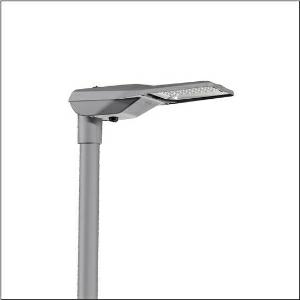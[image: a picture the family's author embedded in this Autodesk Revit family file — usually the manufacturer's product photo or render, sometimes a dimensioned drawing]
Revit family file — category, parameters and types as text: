
# Revit family: streetlight_sl_21_iq_mini___p0_5a_5xe2v31y08jb_f279
name_source: partatom
category: Lighting Fixtures
units: mm (PartAtom-declared; Revit-internal decimal feet)

## family parameters
Cut with Voids When Loaded = No
Host = Face
Light Source = No
Part Type = Normal
Room Calculation Point = No
Round Connector Dimension = Use Diameter
Shared = No

## types (1)
- --- (1 x LED, 11020 lm, 72.5 W, 3000K)
    Apparent Load = 73 VA
    CIE Flux Codes = 37 73 96 100 100
    Color Rendering = 70
    Color Temperature = 3000K
    Default Elevation = 1800 mm
    Description = Streetlight SL 21 iQ mini, mast luminaire, primary light control with lens, of PMMA, primary optical cover: cover, of toughened safety glass, transparent, light distribution: P0.5a, light emission: direct distribution, primary light characteristic: asymmetric, installation type: post-top, side-entry, LED, High Power LED, rated luminous flux: 11.020lm, luminous efficacy: 152lm/W, light colour: 730, colour temperature: 3000K, control gear: iQ-Street Remote, D4i with power reduction, control: pre-setting: logarithmic dimming characteristic, Street-Remote, Auto-Match, Temp-Guard, Lumen-Switch, Night-Set, Smart-Wire, Light-Fading, Desk-Remote (wireless, voltage-free reading and setting of iQ features in the workshop via application-optimized NFC function/RFID function), optimised constant luminous flux control (CLO 2.0), mains connection: 220..240V, AC, 50/60Hz, start of lifetime: 73W, end of service life: 76W, reduction: 33W, luminaire housing, of diecast aluminium, powder-coated, SITECO metallic grey (DB 702S), corrosivity category C5 high according to DIN EN ISO 12944, please order mast flange separately, inclination adjustable: 0°, 5°, 10°, 15°, sealing non-destructively replaceable, multi-level sealing system, length: 628mm, width: 235mm, height: 110mm, mast flange for spigot size: 42mm (side-entry): 5XC10008XM4, 60/48mm (side-entry/post-top): 5XC10108XM2, 76/60mm (side-entry/post-top): 5XC10108XM1, mounting height: 4..8m, Smart Interface below and above, protection rating (complete): IP66, insulation class (complete): insulation class II (safety insulation), certification: CE, ENEC, ENEC+, VDE, impact resistance: IK10, permissible operating ambient temperature for outdoor applications: -40..+50°C, standard-compliant lighting for roads and squares, packaging unit: 1 piece

Light Distribution: P0.5a
    Height = 110 mm
    Lamp = 1 x LED
    Lamp Light Flux = 11020 lm
    Lamp Power = 72.5 W
    Lamp count = 1
    Length = 625 mm
    Luminous efficacy = 152 lm/W
    Manufacturer = Siteco
    ModVariant = No
    Model = 5XE2V31Y08JB
    Number of Poles = 1
    OnlyDefault = Yes
    Power Factor = 1
    Product Name = Streetlight SL 21 iQ mini | P0.5a
    Product group = mast luminaire | pylon top
    ProductGroupID = 6100
    Protection Class = Protection class II
    Protection Degree = IP 66
    RLX_Detail_Level = 1
    RLX_Emergency_Light_Flux = 0 lm
    RLX_Emergency_Type = 0
    RLX_Emergency_Type_DB = No
    RlxData = <blob elided: 92225 chars, md5=cd2c92f3>
    Socket = socket
    Standby Power = 0 W
    System Light Flux = 11020 lm
    System Power = 73 W
    Type Comments = factory setting: luminous flux: 100 % | dim-lin: 254 | 755 mA
    Type Image = l_1003514.jpg
    URL = http://relux.com
    VarID = @adj_077129
    Voltage = 0 V
    Weight = 0.00 kg
    Width = 234 mm

## geometry (parser evidence)
native form markers: Blend x4, Sweep x11
no freeform markers — native parametric forms only
